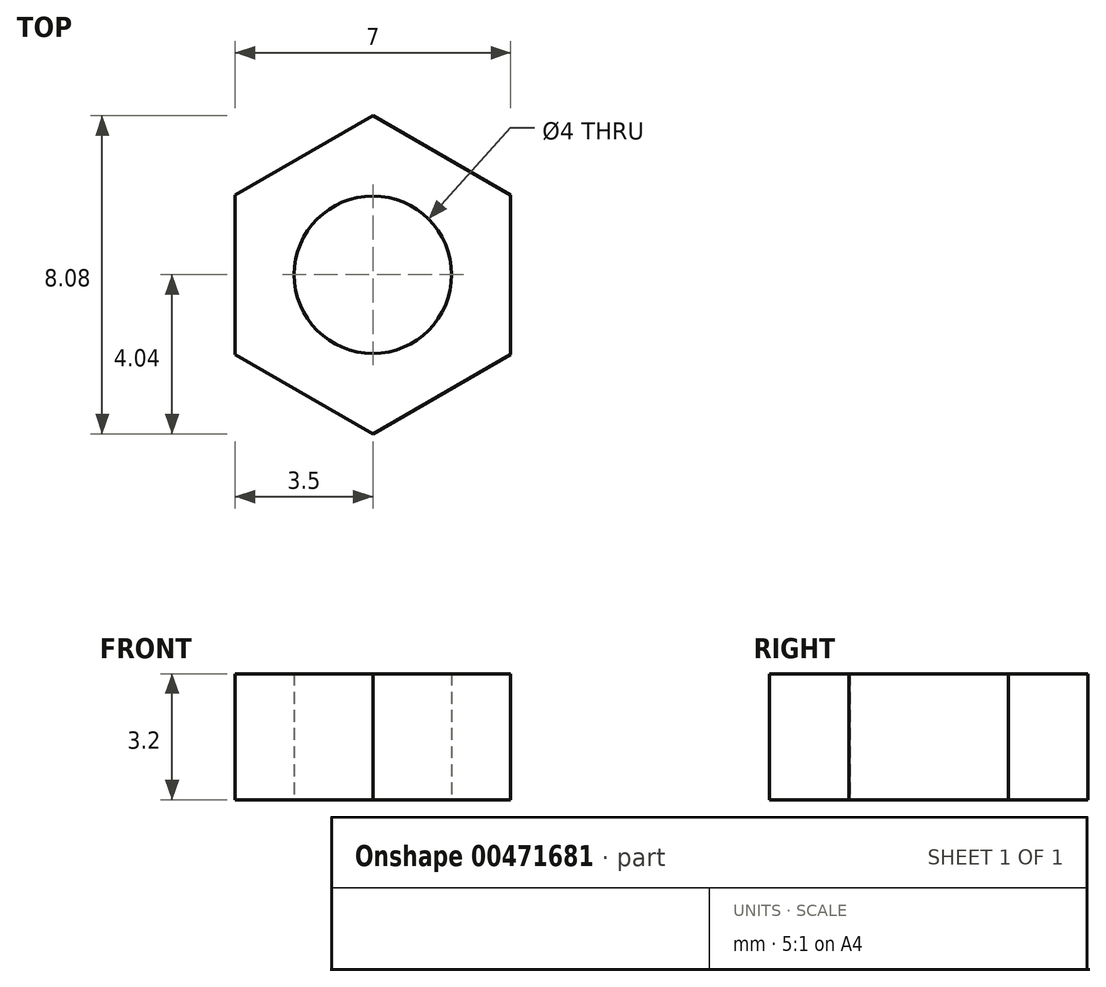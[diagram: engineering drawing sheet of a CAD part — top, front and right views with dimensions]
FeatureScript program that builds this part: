
annotation { "Feature Type Name" : "Feature", "Feature Type Description" : "" }
export const myFeature = defineFeature(function(context is Context, id is Id, definition is map)
    precondition{}
    {
        {
            var Q0;
            Q0=qCreatedBy(makeId("Top.planeOp"),FACE);
            var sketch = newSketch(context, id + "F0", { "sketchPlane" : qUnion([Q0])});
            skCircle(sketch, "E0.cCircle", {"center": v(0, 0) * mm, "radius": 3.5 * mm, "construction": true});
            skLineSegment(sketch, "E0.0", {"start": v(3.5, 2.02) * mm, "end": v(3.5, -2.02) * mm});
            skLineSegment(sketch, "E0.1", {"start": v(3.5, -2.02) * mm, "end": v(0, -4.04) * mm});
            skLineSegment(sketch, "E0.2", {"start": v(0, -4.04) * mm, "end": v(-3.5, -2.02) * mm});
            skLineSegment(sketch, "E0.3", {"start": v(-3.5, -2.02) * mm, "end": v(-3.5, 2.02) * mm});
            skLineSegment(sketch, "E0.4", {"start": v(-3.5, 2.02) * mm, "end": v(0, 4.04) * mm});
            skLineSegment(sketch, "E0.5", {"start": v(0, 4.04) * mm, "end": v(3.5, 2.02) * mm});
            skPoint(sketch, "E0.0.midPoint", {"position": v(3.5, 0) * mm});
            skCircle(sketch, "E1", {"center": v(0, 0) * mm, "radius": 2 * mm});
            skLineSegment(sketch, "E2", {"start": v(7.38, -5.54) * mm, "end": v(13.52, 0.8) * mm});
            skLineSegment(sketch, "E3", {"start": v(20.7, -7.08) * mm, "end": v(9.18, -9.8) * mm});
            skLineSegment(sketch, "E4", {"start": v(16.98, 1.44) * mm, "end": v(22.47, -4.8) * mm});
            skCircle(sketch, "E5", {"center": v(15.47, -3.68) * mm, "radius": 4.52 * mm});
            skPoint(sketch, "E5.first.point", {"position": v(12.22, -0.54) * mm});
            skPoint(sketch, "E5.second.point", {"position": v(18.86, -0.7) * mm});
            skPoint(sketch, "E5.third.point", {"position": v(16.5, -8.07) * mm});
            skSolve(sketch);
        }
        {
            var Q0;
            Q0=makeQuery(id+"F0.imprint","IMPRINT",FACE,{"disambiguationData":[TD([[makeQuery(id+"F0.imprint","IMPRINT",EDGE,{"derivedFrom":sQuery(id+"F0.wireOp",EDGE,"E0.0")}),-1.0]])]});
            extrude(context, id + "F1", {"entities" : qUnion([Q0]), "depth" : 3.2 * mm});
        }
    });
